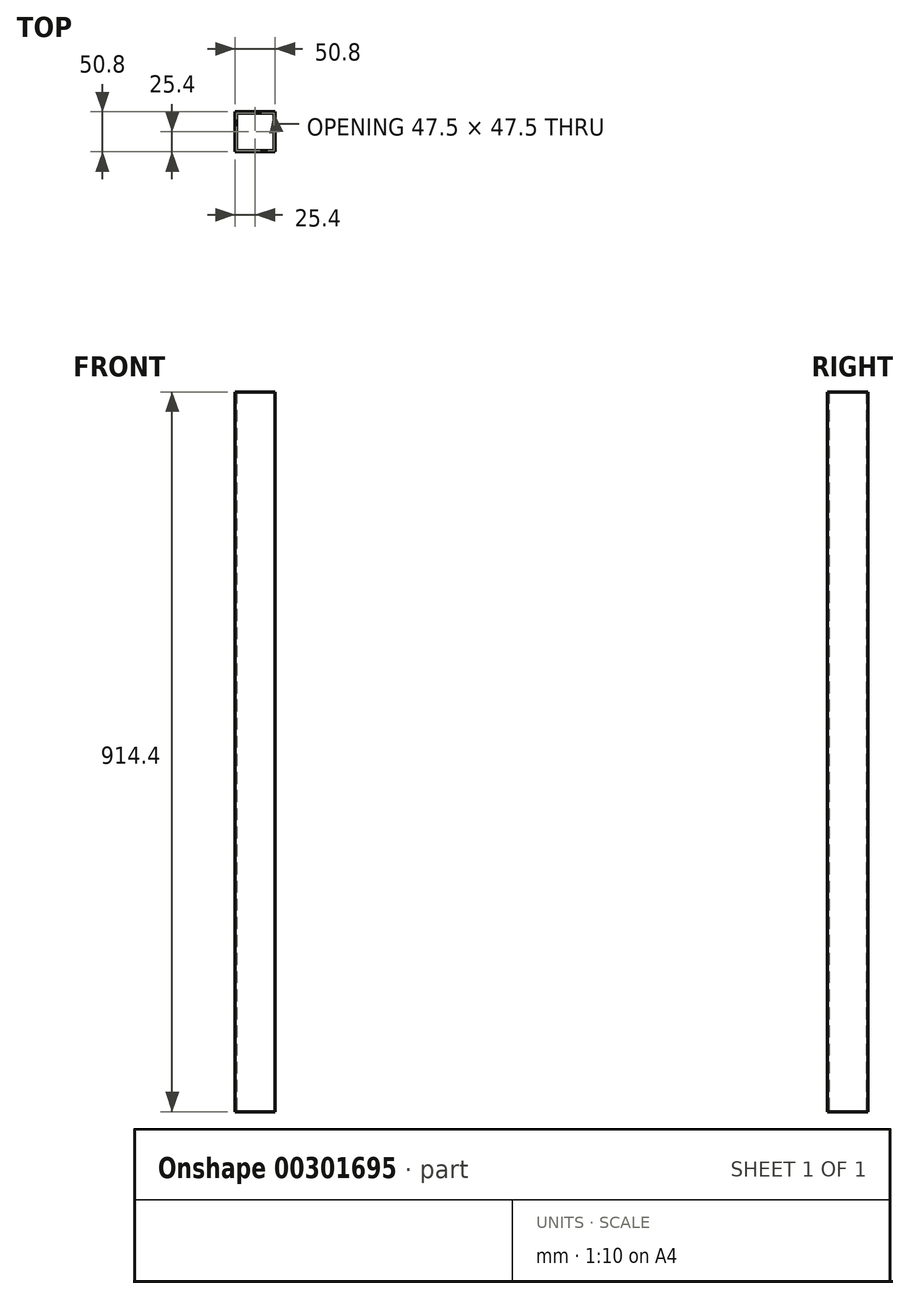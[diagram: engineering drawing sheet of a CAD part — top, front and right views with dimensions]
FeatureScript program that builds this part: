
annotation { "Feature Type Name" : "Feature", "Feature Type Description" : "" }
export const myFeature = defineFeature(function(context is Context, id is Id, definition is map)
    precondition{}
    {
        {
            var Q0;
            Q0=qCreatedBy(makeId("Top.planeOp"),FACE);
            var sketch = newSketch(context, id + "F0", { "sketchPlane" : qUnion([Q0])});
            skLineSegment(sketch, "E0.bottom", {"start": v(25.4, -25.4) * mm, "end": v(-25.4, -25.4) * mm});
            skLineSegment(sketch, "E0.top", {"start": v(25.4, 25.4) * mm, "end": v(-25.4, 25.4) * mm});
            skLineSegment(sketch, "E0.left", {"start": v(25.4, -25.4) * mm, "end": v(25.4, 25.4) * mm});
            skLineSegment(sketch, "E0.right", {"start": v(-25.4, -25.4) * mm, "end": v(-25.4, 25.4) * mm});
            skPoint(sketch, "E0.middle", {"position": v(0, 0) * mm});
            skLineSegment(sketch, "E1.0", {"start": v(22.1, 23.75) * mm, "end": v(-22.1, 23.75) * mm});
            skLineSegment(sketch, "E1.1", {"start": v(23.75, -22.1) * mm, "end": v(23.75, 22.1) * mm});
            skLineSegment(sketch, "E1.2", {"start": v(22.1, -23.75) * mm, "end": v(-22.1, -23.75) * mm});
            skLineSegment(sketch, "E1.3", {"start": v(-23.75, -22.1) * mm, "end": v(-23.75, 22.1) * mm});
            skPoint(sketch, "E2.visualSharp", {"position": v(-23.75, 23.75) * mm});
            skArc(sketch, "E2.filletArc", {"start": v(-22.1, 23.75) * mm, "mid": v(-23.27, 23.27) * mm, "end": v(-23.75, 22.1) * mm});
            skPoint(sketch, "E3.visualSharp", {"position": v(23.75, 23.75) * mm});
            skArc(sketch, "E3.filletArc", {"start": v(23.75, 22.1) * mm, "mid": v(23.27, 23.27) * mm, "end": v(22.1, 23.75) * mm});
            skPoint(sketch, "E4.visualSharp", {"position": v(23.75, -23.75) * mm});
            skArc(sketch, "E4.filletArc", {"start": v(22.1, -23.75) * mm, "mid": v(23.27, -23.27) * mm, "end": v(23.75, -22.1) * mm});
            skPoint(sketch, "E5.visualSharp", {"position": v(-23.75, -23.75) * mm});
            skArc(sketch, "E5.filletArc", {"start": v(-23.75, -22.1) * mm, "mid": v(-23.27, -23.27) * mm, "end": v(-22.1, -23.75) * mm});
            skSolve(sketch);
        }
        {
            var Q0;
            Q0=makeQuery(id+"F0.imprint","IMPRINT",FACE,{"disambiguationData":[TD([[makeQuery(id+"F0.imprint","IMPRINT",EDGE,{"derivedFrom":sQuery(id+"F0.wireOp",EDGE,"E0.bottom")}),-1.0]])]});
            extrude(context, id + "F1", {"entities" : qUnion([Q0]), "depth" : 914.4 * mm});
        }
    });
